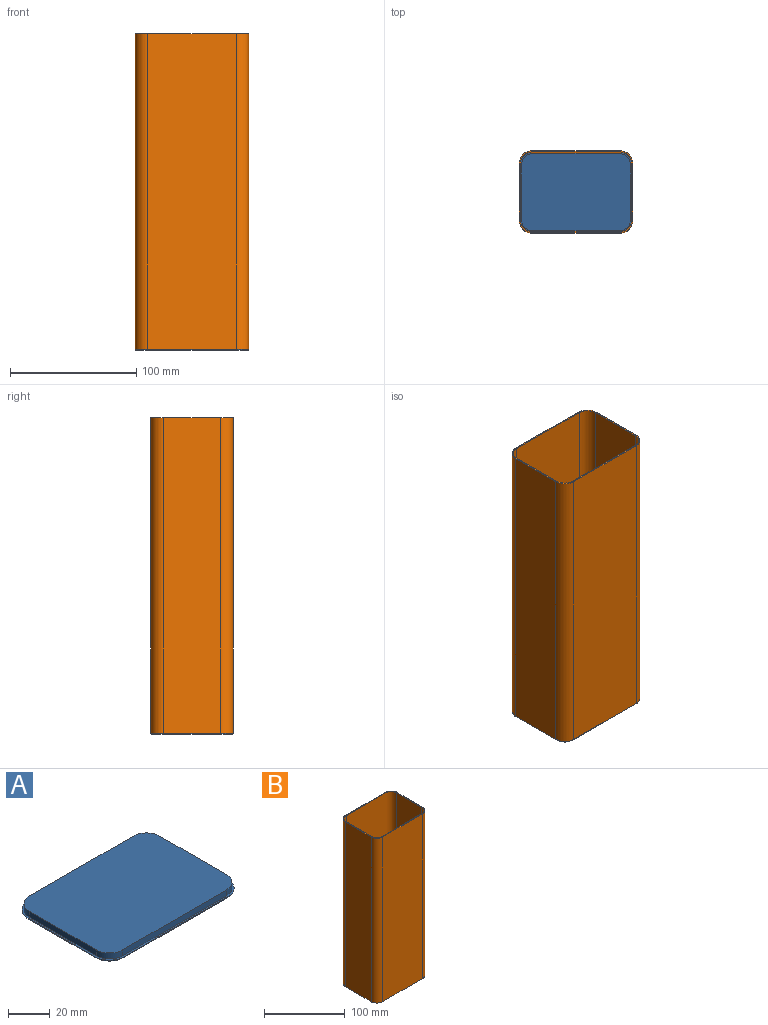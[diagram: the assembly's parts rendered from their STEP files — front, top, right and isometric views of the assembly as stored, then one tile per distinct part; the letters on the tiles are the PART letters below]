
ASSEMBLY  parts=2 mates=1
PART A: 27 faces, bbox 91.6x66.6x4.5 mm
  f0: plane 45x2.5mm, normal (-1,0,0), area 112.5mm2, adj f1,f7,f8,f17
  f1: cylinder r=8mm len=8mm, axis (0,0,-1), area 31.4mm2, adj f0,f2,f8,f10
  f2: plane 70x2.5mm, normal (0,-1,0), area 175mm2, adj f1,f3,f8,f11
  f3: cylinder r=8mm len=8mm, axis (0,0,-1), area 31.4mm2, adj f2,f4,f8,f12
  f4: plane 45x2.5mm, normal (1,0,0), area 112.5mm2, adj f3,f5,f8,f13
  f5: cylinder r=8mm len=8mm, axis (0,0,-1), area 31.4mm2, adj f4,f6,f8,f14
  f6: plane 70x2.5mm, normal (0,1,0), area 175mm2, adj f5,f7,f8,f15
  f7: cylinder r=8mm len=8mm, axis (0,0,-1), area 31.4mm2, adj f0,f6,f8,f16
  f8: plane 86x61mm, normal (0,0,-1), area 5191.1mm2, adj f0,f1,f2,f3,f4,f5,f6,f7
  f9: plane 90x65mm, normal (0,0,1), area 289.7mm2, adj f10,f11,f12,f13,f14,f15,f16,f17
  f10: torus R=9mm, axis (0,0,-1), area 44.4mm2, adj f1,f9,f11,f17
  f11: cylinder r=1mm len=70mm, axis (1,0,0), area 219.9mm2, adj f2,f9,f10,f12
  f12: torus R=9mm, axis (0,0,-1), area 44.4mm2, adj f3,f9,f11,f13
  f13: cylinder r=1mm len=45mm, axis (0,1,0), area 141.4mm2, adj f4,f9,f12,f14
  f14: torus R=9mm, axis (0,0,-1), area 44.4mm2, adj f5,f9,f13,f15
  f15: cylinder r=1mm len=70mm, axis (-1,0,0), area 219.9mm2, adj f6,f9,f14,f16
  f16: torus R=9mm, axis (0,0,-1), area 44.4mm2, adj f7,f9,f15,f17
  f17: cylinder r=1mm len=45mm, axis (0,-1,0), area 141.4mm2, adj f0,f9,f10,f16
  f18: plane 88x63mm, normal (0,0,1), area 5474.5mm2, adj f19,f20,f21,f22,f23,f24,f25,f26
  f19: cylinder r=9mm len=9mm, axis (0,0,-1), area 49.5mm2, adj f9,f18,f20,f26
  f20: plane 70x3.5mm, normal (0,-1,0), area 245mm2, adj f9,f18,f19,f21
  f21: cylinder r=9mm len=9mm, axis (0,0,-1), area 49.5mm2, adj f9,f18,f20,f22
  f22: plane 45x3.5mm, normal (-1,0,0), area 157.5mm2, adj f9,f18,f21,f23
  f23: cylinder r=9mm len=9mm, axis (0,0,-1), area 49.5mm2, adj f9,f18,f22,f24
  f24: plane 70x3.5mm, normal (0,1,0), area 245mm2, adj f9,f18,f23,f25
  f25: cylinder r=9mm len=9mm, axis (0,0,-1), area 49.5mm2, adj f9,f18,f24,f26
  f26: plane 45x3.5mm, normal (1,0,0), area 157.5mm2, adj f9,f18,f19,f25
PART B: 18 faces, bbox 90x65x250 mm
  f0: plane 90x65mm, normal (0,0,1), area 289.7mm2, adj f2,f3,f4,f5,f6,f7,f8,f9
  f1: plane 90x65mm, normal (0,0,-1), area 289.7mm2, adj f2,f3,f4,f5,f6,f7,f8,f9
  f2: plane 250x70mm, normal (0,-1,0), area 17500mm2, adj f0,f1,f3,f9
  f3: cylinder r=10mm len=250mm, axis (0,0,-1), area 3927mm2, adj f0,f1,f2,f4
  f4: plane 250x45mm, normal (1,0,0), area 11250mm2, adj f0,f1,f3,f5
  f5: cylinder r=10mm len=250mm, axis (0,0,-1), area 3927mm2, adj f0,f1,f4,f6
  f6: plane 250x70mm, normal (0,1,0), area 17500mm2, adj f0,f1,f5,f7
  f7: cylinder r=10mm len=250mm, axis (0,0,-1), area 3927mm2, adj f0,f1,f6,f8
  f8: plane 250x45mm, normal (-1,0,0), area 11250mm2, adj f0,f1,f7,f9
  f9: cylinder r=10mm len=250mm, axis (0,0,-1), area 3927mm2, adj f0,f1,f2,f8
  f10: plane 250x70mm, normal (0,1,0), area 17500mm2, adj f0,f1,f11,f17
  f11: cylinder r=9mm len=250mm, axis (0,0,-1), area 3534.3mm2, adj f0,f1,f10,f12
  f12: plane 250x45mm, normal (-1,0,0), area 11250mm2, adj f0,f1,f11,f13
  f13: cylinder r=9mm len=250mm, axis (0,0,-1), area 3534.3mm2, adj f0,f1,f12,f14
  f14: plane 250x70mm, normal (0,-1,0), area 17500mm2, adj f0,f1,f13,f15
  f15: cylinder r=9mm len=250mm, axis (0,0,-1), area 3534.3mm2, adj f0,f1,f14,f16
  f16: plane 250x45mm, normal (1,0,0), area 11250mm2, adj f0,f1,f15,f17
  f17: cylinder r=9mm len=250mm, axis (0,0,-1), area 3534.3mm2, adj f0,f1,f10,f16
PLACE A at identity fixed
PLACE B at identity
MATE fastened B.f5 <-> A.f1  axis (0,0,-1) through (35,22.5,0)mm
